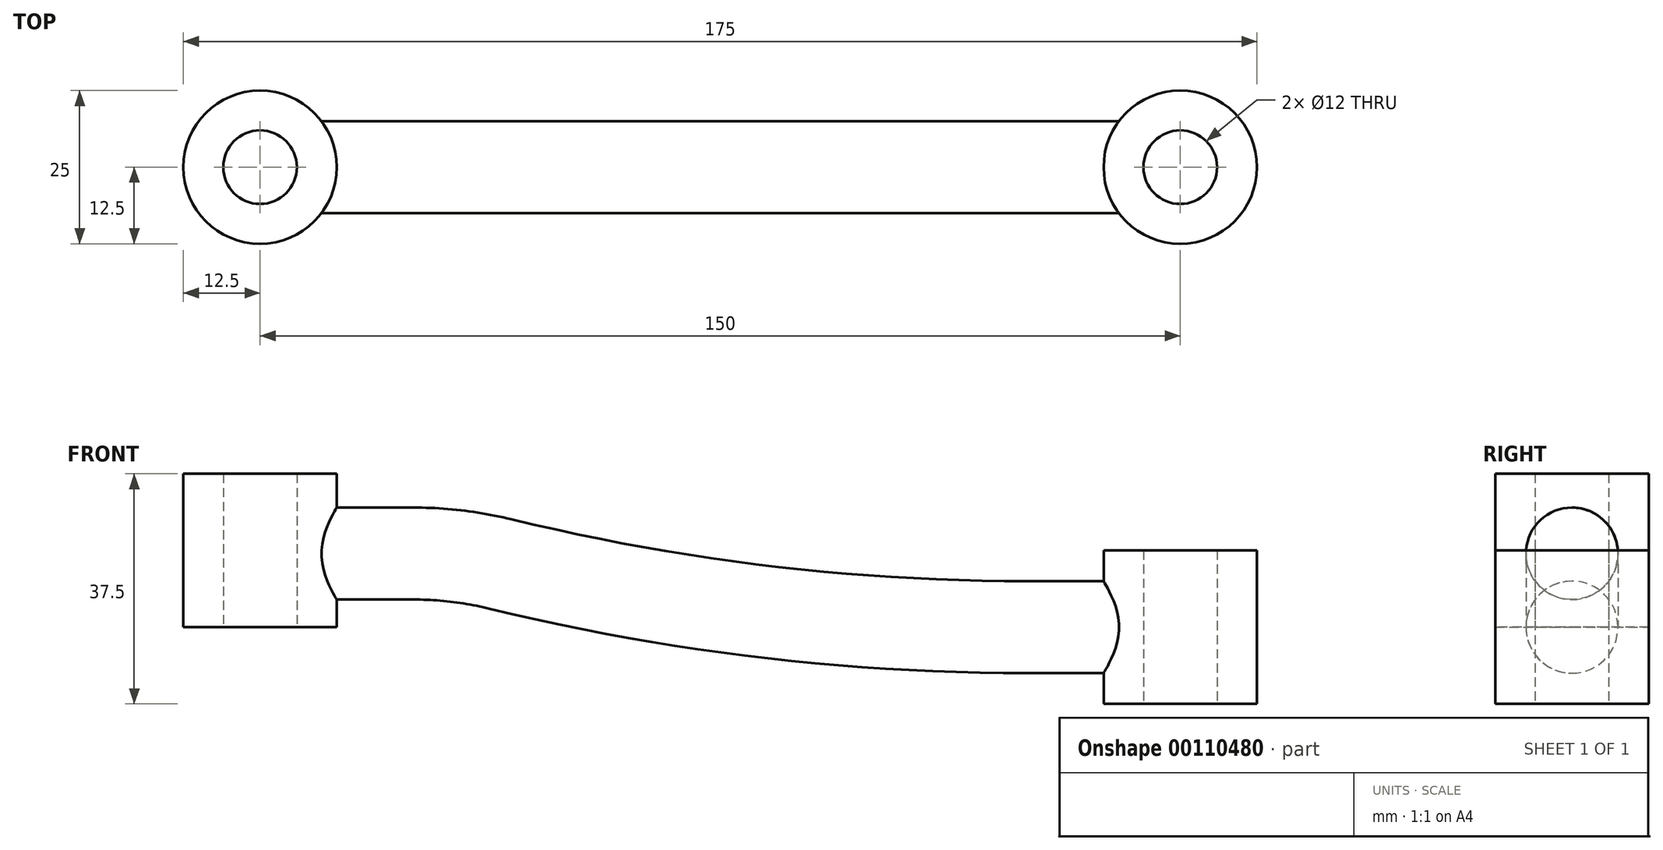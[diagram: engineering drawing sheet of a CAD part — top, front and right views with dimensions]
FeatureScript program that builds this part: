
annotation { "Feature Type Name" : "Feature", "Feature Type Description" : "" }
export const myFeature = defineFeature(function(context is Context, id is Id, definition is map)
    precondition{}
    {
        {
            var Q0;
            Q0=qCreatedBy(makeId("Top.planeOp"),FACE);
            var sketch = newSketch(context, id + "F0", { "sketchPlane" : qUnion([Q0])});
            skCircle(sketch, "E0", {"center": v(0, 0) * mm, "radius": 12.5 * mm});
            skCircle(sketch, "E1", {"center": v(0, 0) * mm, "radius": 6 * mm});
            skLineSegment(sketch, "E2", {"start": v(0, 0) * mm, "end": v(150, 0) * mm, "construction": true});
            skCircle(sketch, "E3", {"center": v(150, 0) * mm, "radius": 12.5 * mm});
            skCircle(sketch, "E4", {"center": v(150, 0) * mm, "radius": 6 * mm});
            skSolve(sketch);
        }
        {
            var Q0;
            Q0=makeQuery(id+"F0.imprint","IMPRINT",FACE,{"disambiguationData":[TD([[makeQuery(id+"F0.imprint","IMPRINT",EDGE,{"derivedFrom":sQuery(id+"F0.wireOp",EDGE,"E0")}),1.0]])]});
            extrude(context, id + "F1", {"entities" : qUnion([Q0]), "depth" : 25 * mm});
        }
        {
            var Q0;
            Q0=makeQuery(id+"F0.imprint","IMPRINT",FACE,{"disambiguationData":[TD([[makeQuery(id+"F0.imprint","IMPRINT",EDGE,{"derivedFrom":sQuery(id+"F0.wireOp",EDGE,"E3")}),1.0]])]});
            var Q1;
            Q1=sQuery(id+"F0.wireOp",EDGE,"E4");
            var Q2;
            Q2=sQuery(id+"F0.wireOp",EDGE,"E3");
            extrude(context, id + "F2", {"entities" : qUnion([Q0]), "surfaceEntities" : qUnion([Q1, Q2]), "depth" : 12.5 * mm, "hasSecondDirection" : true, "secondDirectionOppositeDirection" : true, "secondDirectionDepth" : 12.5 * mm});
        }
        {
            var Q0;
            Q0=qCreatedBy(makeId("Front.planeOp"),FACE);
            var sketch = newSketch(context, id + "F3", { "sketchPlane" : qUnion([Q0])});
            skLineSegment(sketch, "E5", {"start": v(0, 0) * mm, "end": v(0, 12) * mm, "construction": true});
            skLineSegment(sketch, "E6", {"start": v(0, 12) * mm, "end": v(25, 12) * mm});
            skLineSegment(sketch, "E7", {"start": v(150, 0) * mm, "end": v(125, 0) * mm});
            skArc(sketch, "E8", {"start": v(25, 12) * mm, "mid": v(32.15, 11.57) * mm, "end": v(39.2, 10.3) * mm});
            skArc(sketch, "E9", {"start": v(125, 0) * mm, "mid": v(81.79, 2.58) * mm, "end": v(39.2, 10.3) * mm});
            skLineSegment(sketch, "E10", {"start": v(0, 0) * mm, "end": v(150, 0) * mm, "construction": true});
            skSolve(sketch);
        }
        {
            var Q0;
            Q0=qCreatedBy(makeId("Right.planeOp"),FACE);
            var sketch = newSketch(context, id + "F4", { "sketchPlane" : qUnion([Q0])});
            skCircle(sketch, "E11", {"center": v(0, 12) * mm, "radius": 7.5 * mm});
            skSolve(sketch);
        }
        {
            var Q0;
            Q0 = qSketchRegion(id + "F4", true);
            var Q1;
            Q1 = qConstructionFilter(qBodyType(qCreatedBy(id + "F3" ,EDGE), BodyType.WIRE), ConstructionObject.NO);
            sweep(context, id + "F5", {"operationType" : NewBodyOperationType.ADD, "profiles" : qUnion([Q0]), "path" : qUnion([Q1])});
        }
        {
            var Q0;
            Q0=makeQuery(id+"F1.opExtrude","CAP_FACE",FACE,{"disambiguationData":[OSD([sQuery(id+"F0.wireOp",EDGE,"E0"),sQuery(id+"F0.wireOp",EDGE,"E1")])],"isStart":false});
            var sketch = newSketch(context, id + "F6", { "sketchPlane" : qUnion([Q0])});
            skCircle(sketch, "E12.0", {"center": v(0, 0) * mm, "radius": 6 * mm});
            skSolve(sketch);
        }
        {
            var Q0;
            Q0 = qSketchRegion(id + "F6", true);
            extrude(context, id + "F7", {"entities" : qUnion([Q0]), "operationType" : NewBodyOperationType.REMOVE, "endBound" : BoundingType.THROUGH_ALL, "oppositeDirection" : true, "depth" : 25 * mm});
        }
        {
            var Q0;
            Q0=makeQuery(id+"F2.opExtrude","CAP_FACE",FACE,{"disambiguationData":[OSD([sQuery(id+"F0.wireOp",EDGE,"E3"),sQuery(id+"F0.wireOp",EDGE,"E4")])],"isStart":false});
            var sketch = newSketch(context, id + "F8", { "sketchPlane" : qUnion([Q0])});
            skCircle(sketch, "E13.0", {"center": v(150, 0) * mm, "radius": 6 * mm});
            skSolve(sketch);
        }
        {
            var Q0;
            Q0=makeQuery(id+"F8.imprint","IMPRINT",FACE,{"disambiguationData":[TD([[makeQuery(id+"F8.imprint","IMPRINT",EDGE,{"derivedFrom":sQuery(id+"F8.wireOp",EDGE,"E13.0")}),1.0]])]});
            extrude(context, id + "F9", {"entities" : qUnion([Q0]), "operationType" : NewBodyOperationType.REMOVE, "endBound" : BoundingType.THROUGH_ALL, "oppositeDirection" : true, "depth" : 25 * mm});
        }
    });
